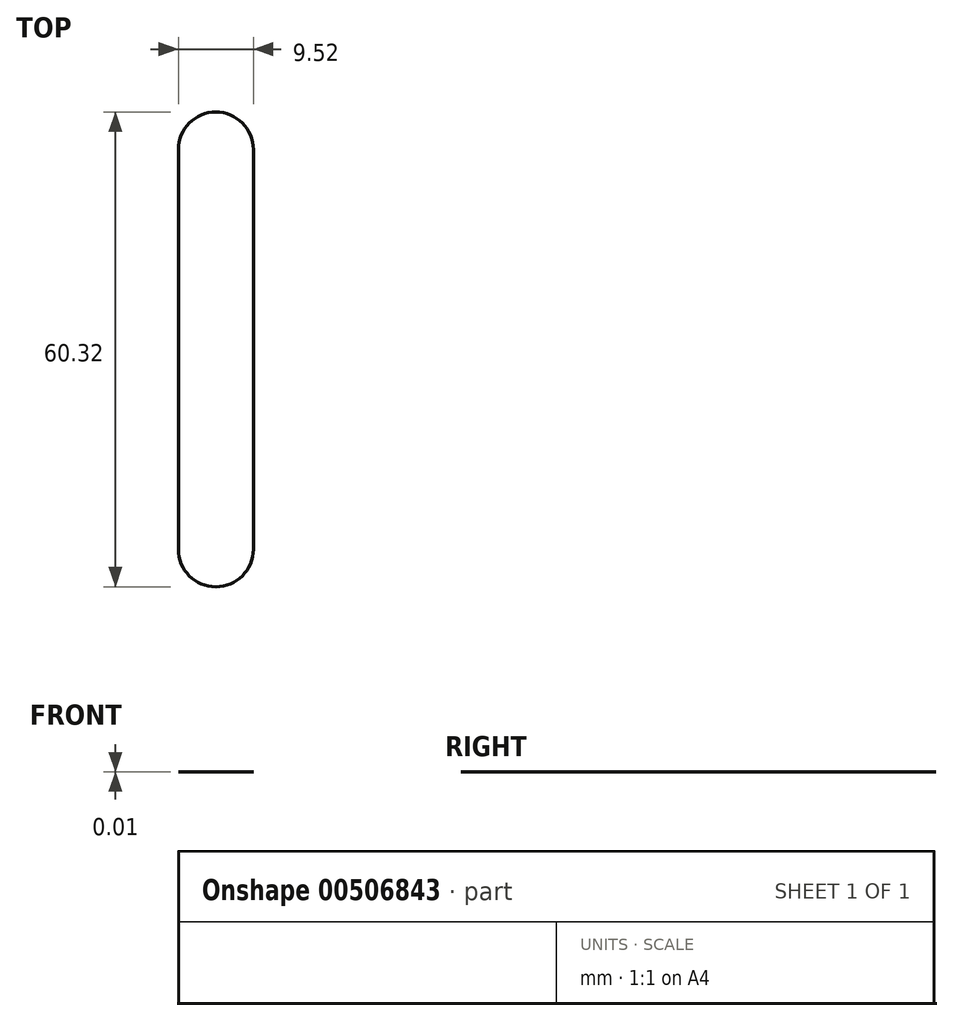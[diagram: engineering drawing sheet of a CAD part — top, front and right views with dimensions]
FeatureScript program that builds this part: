
annotation { "Feature Type Name" : "Feature", "Feature Type Description" : "" }
export const myFeature = defineFeature(function(context is Context, id is Id, definition is map)
    precondition{}
    {
        {
            var Q0;
            Q0=qCreatedBy(makeId("Top.planeOp"),FACE);
            var sketch = newSketch(context, id + "F0", { "sketchPlane" : qUnion([Q0])});
            skLineSegment(sketch, "E0", {"start": v(-55.54, 22.35) * mm, "end": v(-55.54, -28.45) * mm});
            skLineSegment(sketch, "E1", {"start": v(-46.02, 22.35) * mm, "end": v(-46.02, -28.45) * mm});
            skArc(sketch, "E2", {"start": v(-46.02, 22.35) * mm, "mid": v(-50.78, 27.11) * mm, "end": v(-55.54, 22.35) * mm});
            skArc(sketch, "E3", {"start": v(-55.54, -28.45) * mm, "mid": v(-50.78, -33.21) * mm, "end": v(-46.02, -28.45) * mm});
            skSolve(sketch);
        }
        {
            var Q0;
            Q0=makeQuery(id+"F0.imprint","IMPRINT",FACE,{"disambiguationData":[TD([[makeQuery(id+"F0.imprint","IMPRINT",EDGE,{"derivedFrom":sQuery(id+"F0.wireOp",EDGE,"E0")}),1.0]])]});
            extrude(context, id + "F1", {"entities" : qUnion([Q0]), "depth" : 3 / 203.2 * mm, "offsetDistance" : 25.4 * mm});
        }
    });
